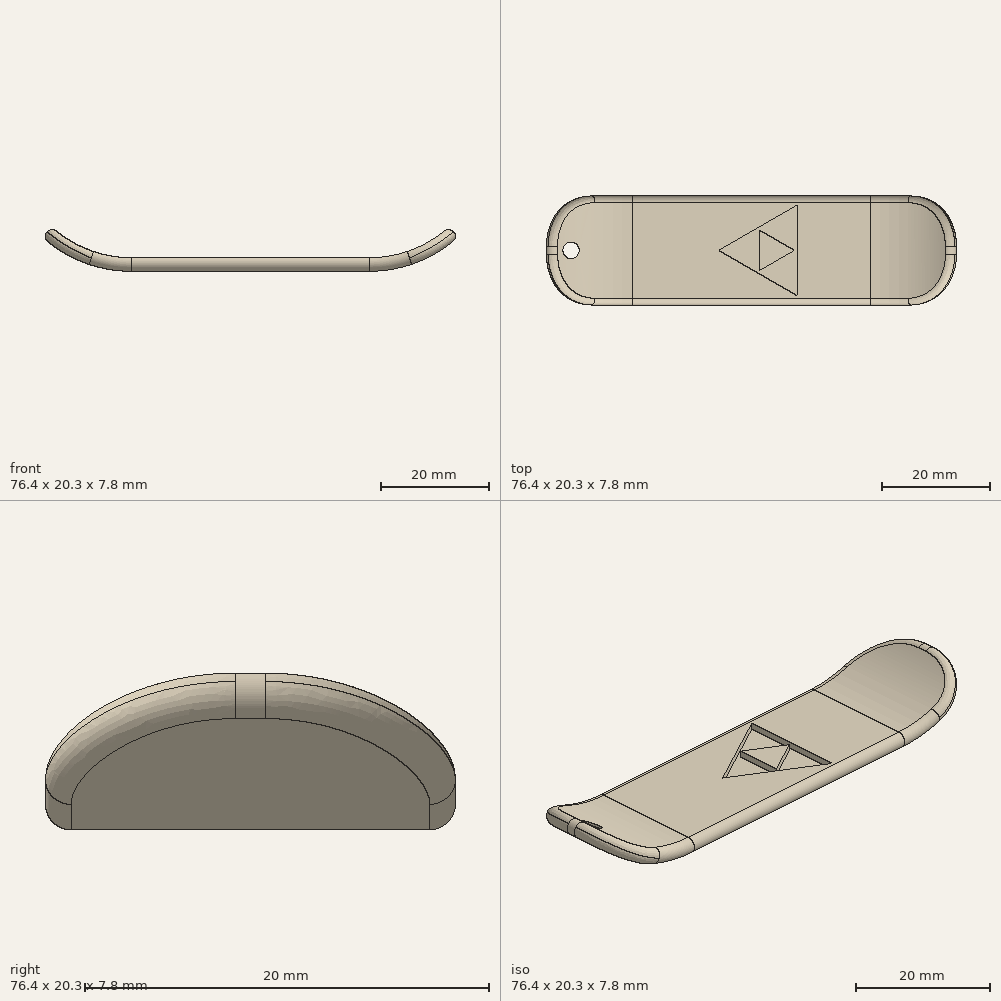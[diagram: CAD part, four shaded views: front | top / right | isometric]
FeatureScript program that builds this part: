
annotation { "Feature Type Name" : "Feature", "Feature Type Description" : "" }
export const myFeature = defineFeature(function(context is Context, id is Id, definition is map)
    precondition{}
    {
        {
            var Q0;
            Q0=qCreatedBy(makeId("Front.planeOp"),FACE);
            var sketch = newSketch(context, id + "F0", { "sketchPlane" : qUnion([Q0])});
            skLineSegment(sketch, "E0", {"start": v(-22.22, 0) * mm, "end": v(22.22, 0) * mm});
            skArc(sketch, "E1", {"start": v(-38.73, 6.39) * mm, "mid": v(-31.08, 1.65) * mm, "end": v(-22.22, 0) * mm});
            skArc(sketch, "E2.MirrorCS", {"start": v(38.73, 6.39) * mm, "mid": v(31.08, 1.65) * mm, "end": v(22.23, 0) * mm});
            skArc(sketch, "E3.0", {"start": v(37.03, 8.27) * mm, "mid": v(30.16, 4.02) * mm, "end": v(22.22, 2.54) * mm});
            skLineSegment(sketch, "E3.1", {"start": v(-22.22, 2.54) * mm, "end": v(22.22, 2.54) * mm});
            skArc(sketch, "E3.2", {"start": v(-37.03, 8.27) * mm, "mid": v(-30.16, 4.02) * mm, "end": v(-22.22, 2.54) * mm});
            skLineSegment(sketch, "E4", {"start": v(-38.73, 6.39) * mm, "end": v(-37.03, 8.27) * mm});
            skLineSegment(sketch, "E5", {"start": v(37.03, 8.27) * mm, "end": v(38.73, 6.39) * mm});
            skSolve(sketch);
        }
        {
            var Q0;
            Q0=qSketchRegion(id+"F0",true);
            extrude(context, id + "F1", {"entities" : qUnion([Q0]), "endBound" : BoundingType.SYMMETRIC, "depth" : 20.32 * mm});
        }
        {
            var Q0;
            Q0=makeQuery(id+"F1.opExtrude","CAP_EDGE",EDGE,{"disambiguationData":[OSD([sQuery(id+"F0.wireOp",EDGE,"E4")])],"isStart":false});
            var Q1;
            Q1=makeQuery(id+"F1.opExtrude","CAP_EDGE",EDGE,{"disambiguationData":[OSD([sQuery(id+"F0.wireOp",EDGE,"E4")])],"isStart":true});
            var Q2;
            Q2=makeQuery(id+"F1.opExtrude","CAP_EDGE",EDGE,{"disambiguationData":[OSD([sQuery(id+"F0.wireOp",EDGE,"E5")])],"isStart":true});
            var Q3;
            Q3=makeQuery(id+"F1.opExtrude","CAP_EDGE",EDGE,{"disambiguationData":[OSD([sQuery(id+"F0.wireOp",EDGE,"E5")])],"isStart":false});
            fillet(context, id + "F2", {"entities" : qUnion([Q0, Q1, Q2, Q3]), "radius" : 9.4 * mm, "tangentPropagation" : true, "allowEdgeOverflow" : false});
        }
        {
            var Q0;
            Q0=makeQuery(id+"F1.opExtrude","CAP_EDGE",EDGE,{"disambiguationData":[OSD([sQuery(id+"F0.wireOp",EDGE,"E3.2")])],"isStart":false});
            var Q1;
            Q1=makeQuery(id+"F2.opFillet","BLEND_EDGE",EDGE,{"blendedFrom":[makeQuery(id+"F1.opExtrude","CAP_EDGE",EDGE,{"disambiguationData":[OSD([sQuery(id+"F0.wireOp",EDGE,"E4")])],"isStart":false}),makeQuery(id+"F1.opExtrude","SWEPT_FACE",FACE,{"disambiguationData":[OSD([sQuery(id+"F0.wireOp",EDGE,"E1")])]})],"blendedInto":[makeQuery(id+"F1.opExtrude","SWEPT_FACE",FACE,{"disambiguationData":[OSD([sQuery(id+"F0.wireOp",EDGE,"E1")])]})]});
            fillet(context, id + "F3", {"entities" : qUnion([Q0, Q1]), "radius" : 1.27 * mm, "tangentPropagation" : true, "allowEdgeOverflow" : false});
        }
        {
            var Q0;
            Q0=qCreatedBy(makeId("Top.planeOp"),FACE);
            var sketch = newSketch(context, id + "F4", { "sketchPlane" : qUnion([Q0])});
            skPoint(sketch, "E6.0", {"position": v(-38.18, 0.76) * mm});
            skCircle(sketch, "E7", {"center": v(-33.61, 0) * mm, "radius": 1.52 * mm});
            skSolve(sketch);
        }
        {
            var Q0;
            Q0=qSketchRegion(id+"F4",true);
            extrude(context, id + "F5", {"entities" : qUnion([Q0]), "operationType" : NewBodyOperationType.REMOVE, "depth" : 25.4 * mm});
        }
        {
            var Q0;
            Q0=makeQuery(id+"F1.opExtrude","SWEPT_FACE",FACE,{"disambiguationData":[OSD([sQuery(id+"F0.wireOp",EDGE,"E3.1")])]});
            var sketch = newSketch(context, id + "F6", { "sketchPlane" : qUnion([Q0])});
            skLineSegment(sketch, "E8", {"start": v(8.8, -8.9) * mm, "end": v(8.8, 8.9) * mm, "construction": true});
            skLineSegment(sketch, "E9", {"start": v(8.8, 8.9) * mm, "end": v(-6.59, 0) * mm, "construction": true});
            skLineSegment(sketch, "E10", {"start": v(-6.59, 0) * mm, "end": v(8.8, -8.9) * mm, "construction": true});
            skLineSegment(sketch, "E11.0", {"start": v(8.55, -8.45) * mm, "end": v(8.55, 8.45) * mm});
            skLineSegment(sketch, "E11.1", {"start": v(-6.08, 0) * mm, "end": v(8.55, -8.45) * mm});
            skLineSegment(sketch, "E11.2", {"start": v(8.55, 8.45) * mm, "end": v(-6.08, 0) * mm});
            skLineSegment(sketch, "E12", {"start": v(1.24, -4.23) * mm, "end": v(8.55, 0) * mm, "construction": true});
            skLineSegment(sketch, "E13", {"start": v(8.55, 0) * mm, "end": v(1.24, 4.23) * mm, "construction": true});
            skLineSegment(sketch, "E14", {"start": v(1.24, 4.23) * mm, "end": v(1.24, -4.23) * mm, "construction": true});
            skLineSegment(sketch, "E15.0", {"start": v(1.5, 3.79) * mm, "end": v(1.5, -3.79) * mm});
            skLineSegment(sketch, "E15.1", {"start": v(8.05, 0) * mm, "end": v(1.5, 3.79) * mm});
            skLineSegment(sketch, "E15.2", {"start": v(1.5, -3.79) * mm, "end": v(8.05, 0) * mm});
            skSolve(sketch);
        }
        {
            var Q0;
            Q0=makeQuery(id+"F6.imprint","IMPRINT",FACE,{"disambiguationData":[TD([[makeQuery(id+"F6.imprint","IMPRINT",EDGE,{"derivedFrom":sQuery(id+"F6.wireOp",EDGE,"E11.0")}),1.0]])]});
            extrude(context, id + "F7", {"entities" : qUnion([Q0]), "operationType" : NewBodyOperationType.REMOVE, "oppositeDirection" : true, "depth" : 1.02 * mm});
        }
    });
